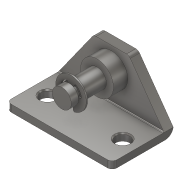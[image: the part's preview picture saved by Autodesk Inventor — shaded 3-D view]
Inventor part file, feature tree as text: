
AUTODESK INVENTOR PART (.ipt)
format: ipt  version: 2019.4 (Build 234330000, 330)  size: 176,128 bytes
history: native  units: in
note: dims shown in document units (in); Inventor stores cm internally (conversion verified against a paired STEP export)
features: fillet x2
ambient origin geometry x8: Origin, YZ Plane, XZ Plane, XY Plane, X Axis, Y Axis, Z Axis, Center Point
bodies: Solid1 (feature_tree), Solid2 (feature_tree)
feature tree (2):
  fillet  "Fillet2"  [1 undecoded]
  fillet  "Fillet5"  [1 undecoded]
note: 2 required parameter values undecoded (feature->parameter linkage not recoverable at this tier; creation-order binding heuristic only, values carry confidence <= 0.55)
